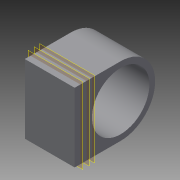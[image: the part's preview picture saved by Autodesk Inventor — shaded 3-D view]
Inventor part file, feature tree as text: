
AUTODESK INVENTOR PART (.ipt)
format: ipt  version: 2014 (Build 180170000, 170)  size: 115,712 bytes
history: native  units: mm
features: sketch x4, plane x3, extrude x2, fillet x2, hole x2
ambient origin geometry x8: Origin, YZ Plane, XZ Plane, XY Plane, X Axis, Y Axis, Z Axis, Center Point
bodies: Volumenkörper1 (feature_tree)
feature tree (13):
  extrude  "Extrusion1"  Depth=36.0mm
  fillet  "Rundung1"  Radius=26.0mm
  hole  "Bohrung1"  [1 undecoded]
  plane  "Arbeitsebene2"
  plane  "Arbeitsebene3"
  extrude  "Extrusion2"  [1 undecoded]
  fillet  "Rundung2"  [1 undecoded]
  plane  "Arbeitsebene6"
  hole  "Bohrung4"  [1 undecoded]
  sketch  "Skizze1"  dims[d0=42.0mm d1=36.0mm d2=26.0mm d3=0.0mm]
  sketch  "Skizze2"  dims[d4=18.0mm d5=30.0mm]
  sketch  "Skizze3"  dims[d6=30.0mm d7=6.0mm d8=4.0mm d9=2.0mm d10=90.0deg d11=8.0mm d12=20.594885mm d13=-3.0mm d14=-6.2mm]
  sketch  "Skizze8"  dims[d15=20.0mm d16=25.0mm d17=0.0mm d18=0.0mm d19=9.0mm d39=13.0mm d40=18.0mm d41=4.2mm d42=6.0mm d43=10.0mm d44=2.0mm d45=90.0deg d46=15.0mm d47=0.0mm]
note: 4 required parameter values undecoded (feature->parameter linkage not recoverable at this tier; creation-order binding heuristic only, values carry confidence <= 0.55)
